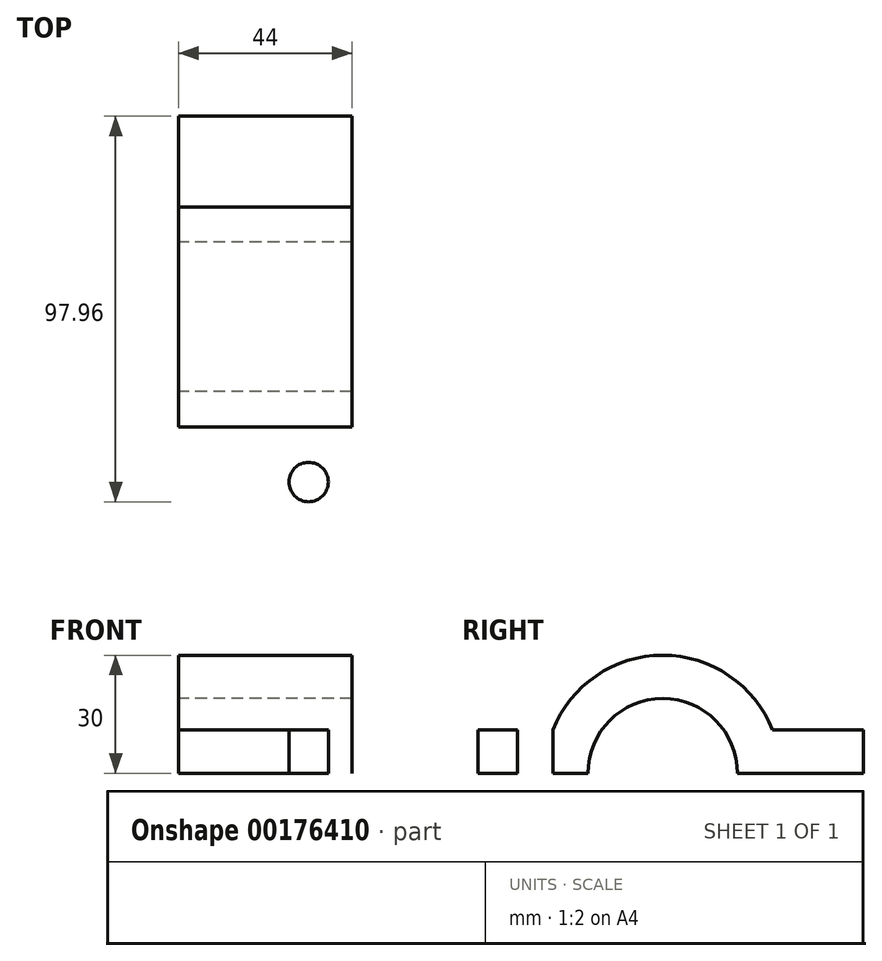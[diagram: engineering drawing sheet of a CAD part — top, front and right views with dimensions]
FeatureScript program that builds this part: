
annotation { "Feature Type Name" : "Feature", "Feature Type Description" : "" }
export const myFeature = defineFeature(function(context is Context, id is Id, definition is map)
    precondition{}
    {
        {
            var Q0;
            Q0=qCreatedBy(makeId("Right.planeOp"),FACE);
            var sketch = newSketch(context, id + "F0", { "sketchPlane" : qUnion([Q0])});
            skCircle(sketch, "E0", {"center": v(0, 0) * mm, "radius": 30 * mm});
            skCircle(sketch, "E1", {"center": v(0, 0) * mm, "radius": 19 * mm});
            skLineSegment(sketch, "E2.bottom", {"start": v(-56, 0) * mm, "end": v(51, 0) * mm});
            skLineSegment(sketch, "E2.top", {"start": v(-56, 11) * mm, "end": v(51, 11) * mm});
            skLineSegment(sketch, "E2.left", {"start": v(-56, 0) * mm, "end": v(-56, 11) * mm});
            skLineSegment(sketch, "E2.right", {"start": v(51, 0) * mm, "end": v(51, 11) * mm});
            skLineSegment(sketch, "E3.bottom", {"start": v(51, 11) * mm, "end": v(40, 11) * mm});
            skLineSegment(sketch, "E3.top", {"start": v(51, 41) * mm, "end": v(40, 41) * mm});
            skLineSegment(sketch, "E3.left", {"start": v(51, 11) * mm, "end": v(51, 41) * mm});
            skLineSegment(sketch, "E3.right", {"start": v(40, 11) * mm, "end": v(40, 41) * mm});
            skSolve(sketch);
        }
        {
            var Q0;
            {var subQ5=sQuery(id+"F0.wireOp",EDGE,"E2.left");Q0=makeQuery(id+"F0.imprint","IMPRINT",FACE,{"disambiguationData":[TD([[makeQuery(id+"F0.imprint","IMPRINT",EDGE,{"derivedFrom":subQ5}),-1.0]])]});}
            var Q1;
            {var subQ0=sQuery(id+"F0.wireOp",EDGE,"E2.top");var subQ1=sQuery(id+"F0.wireOp",EDGE,"E0");var subQ2=makeQuery(id+"F0.imprint","INTERSECT",VERTEX,{"disambiguationData":[OD(1.0)],"derivedFrom":[subQ1,subQ0]});Q1=makeQuery(id+"F0.imprint","IMPRINT",FACE,{"disambiguationData":[TD([[makeQuery(id+"F0.imprint","IMPRINT",EDGE,{"disambiguationData":[TD([[subQ2,-1.0]])],"derivedFrom":subQ1}),1.0]])]});}
            var Q2;
            {var subQ0=sQuery(id+"F0.wireOp",EDGE,"E2.top");var subQ1=sQuery(id+"F0.wireOp",EDGE,"E0");var subQ2=makeQuery(id+"F0.imprint","INTERSECT",VERTEX,{"disambiguationData":[OD(0.0)],"derivedFrom":[subQ1,subQ0]});Q2=makeQuery(id+"F0.imprint","IMPRINT",FACE,{"disambiguationData":[TD([[makeQuery(id+"F0.imprint","IMPRINT",EDGE,{"disambiguationData":[TD([[subQ2,-1.0]])],"derivedFrom":subQ1}),1.0]])]});}
            var Q3;
            {var subQ0=sQuery(id+"F0.wireOp",EDGE,"E2.top");var subQ1=sQuery(id+"F0.wireOp",EDGE,"E0");var subQ2=makeQuery(id+"F0.imprint","INTERSECT",VERTEX,{"disambiguationData":[OD(0.0)],"derivedFrom":[subQ1,subQ0]});Q3=makeQuery(id+"F0.imprint","IMPRINT",FACE,{"disambiguationData":[TD([[makeQuery(id+"F0.imprint","IMPRINT",EDGE,{"disambiguationData":[TD([[subQ2,1.0]])],"derivedFrom":subQ1}),1.0]])]});}
            var Q4;
            {var subQ0=sQuery(id+"F0.wireOp",EDGE,"E2.right");Q4=makeQuery(id+"F0.imprint","IMPRINT",FACE,{"disambiguationData":[TD([[makeQuery(id+"F0.imprint","IMPRINT",EDGE,{"derivedFrom":subQ0}),1.0]])]});}
            var Q5;
            Q5=makeQuery(id+"F0.imprint","IMPRINT",FACE,{"disambiguationData":[TD([[makeQuery(id+"F0.imprint","IMPRINT",EDGE,{"derivedFrom":sQuery(id+"F0.wireOp",EDGE,"E3.bottom")}),-1.0]])]});
            extrude(context, id + "F1", {"entities" : qUnion([Q0, Q1, Q2, Q3, Q4, Q5]), "endBound" : BoundingType.SYMMETRIC, "depth" : 44 * mm});
        }
        {
            var Q0;
            Q0=makeQuery(id+"F1.opExtrude","SWEPT_FACE",FACE,{"disambiguationData":[OSD([sQuery(id+"F0.wireOp",EDGE,"E2.right"),sQuery(id+"F0.wireOp",EDGE,"E3.left")])]});
            var sketch = newSketch(context, id + "F2", { "sketchPlane" : qUnion([Q0])});
            skCircle(sketch, "E4", {"center": v(0, 25) * mm, "radius": 6.5 * mm});
            skLineSegment(sketch, "E5.bottom", {"start": v(-6.5, 25) * mm, "end": v(6.5, 25) * mm});
            skLineSegment(sketch, "E5.top", {"start": v(-6.5, 41) * mm, "end": v(6.5, 41) * mm});
            skLineSegment(sketch, "E5.left", {"start": v(-6.5, 25) * mm, "end": v(-6.5, 41) * mm});
            skLineSegment(sketch, "E5.right", {"start": v(6.5, 25) * mm, "end": v(6.5, 41) * mm});
            skSolve(sketch);
        }
        {
            var Q0;
            Q0=makeQuery(id+"F2.imprint","IMPRINT",FACE,{"disambiguationData":[TD([[makeQuery(id+"F2.imprint","IMPRINT",EDGE,{"derivedFrom":sQuery(id+"F2.wireOp",EDGE,"E5.top")}),-1.0]])]});
            var Q1;
            {var subQ0=sQuery(id+"F2.wireOp",EDGE,"E5.bottom");Q1=makeQuery(id+"F2.imprint","IMPRINT",FACE,{"disambiguationData":[TD([[makeQuery(id+"F2.imprint","IMPRINT",EDGE,{"derivedFrom":subQ0}),1.0]])]});}
            var Q2;
            {var subQ0=sQuery(id+"F2.wireOp",EDGE,"E5.bottom");Q2=makeQuery(id+"F2.imprint","IMPRINT",FACE,{"disambiguationData":[TD([[makeQuery(id+"F2.imprint","IMPRINT",EDGE,{"derivedFrom":subQ0}),-1.0]])]});}
            extrude(context, id + "F3", {"entities" : qUnion([Q0, Q1, Q2]), "operationType" : NewBodyOperationType.REMOVE, "oppositeDirection" : true, "depth" : 25 * mm});
        }
        {
            var Q0;
            {var subQ0=sQuery(id+"F0.wireOp",EDGE,"E2.top");Q0=makeQuery(id+"F1.opExtrude","SWEPT_FACE",FACE,{"disambiguationData":[OSD([subQ0]),TDD([makeQuery(id+"F0.imprint","IMPRINT",EDGE,{"disambiguationData":[TD([[makeQuery(id+"F0.imprint","INTERSECT",VERTEX,{"derivedFrom":[subQ0,sQuery(id+"F0.wireOp",EDGE,"E2.left")]}),-1.0]])],"derivedFrom":subQ0})])]});}
            var sketch = newSketch(context, id + "F4", { "sketchPlane" : qUnion([Q0])});
            skLineSegment(sketch, "E6", {"start": v(-22, -41.96) * mm, "end": v(22, -41.96) * mm, "construction": true});
            skLineSegment(sketch, "E7", {"start": v(0, -27.91) * mm, "end": v(0, -56) * mm, "construction": true});
            skCircle(sketch, "E8", {"center": v(-11, -41.96) * mm, "radius": 5 * mm});
            skCircle(sketch, "E9.MirrorC", {"center": v(11, -41.96) * mm, "radius": 5 * mm});
            skSolve(sketch);
        }
        {
            var Q0;
            Q0=makeQuery(id+"F4.imprint","IMPRINT",FACE,{"disambiguationData":[TD([[makeQuery(id+"F4.imprint","IMPRINT",EDGE,{"derivedFrom":sQuery(id+"F4.wireOp",EDGE,"E8")}),1.0]])]});
            var Q1;
            Q1=makeQuery(id+"F4.imprint","IMPRINT",FACE,{"disambiguationData":[TD([[makeQuery(id+"F4.imprint","IMPRINT",EDGE,{"derivedFrom":sQuery(id+"F4.wireOp",EDGE,"E9.MirrorC")}),-1.0]])]});
            extrude(context, id + "F5", {"entities" : qUnion([Q0, Q1]), "operationType" : NewBodyOperationType.REMOVE, "endBound" : BoundingType.UP_TO_NEXT, "oppositeDirection" : true, "depth" : 25 * mm});
        }
    });
